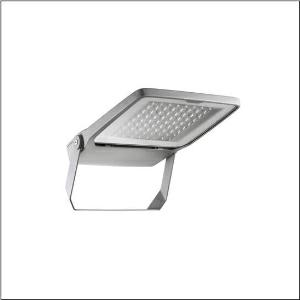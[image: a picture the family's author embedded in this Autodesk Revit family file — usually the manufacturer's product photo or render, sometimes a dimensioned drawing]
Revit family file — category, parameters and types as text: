
# Revit family: floodlight_fl_20_mini___pl43_5xa7671c2a1ac_d5d9
name_source: partatom
category: Lighting Fixtures
units: mm (PartAtom-declared; Revit-internal decimal feet)

## family parameters
Cut with Voids When Loaded = No
Host = Face
Light Source = No
Part Type = Normal
Room Calculation Point = No
Round Connector Dimension = Use Diameter
Shared = No

## types (1)
- Floodlight FL 20 mini  PL43 (1 x LED 4000K / CRI = 70 (unbekannt), 13030 lm, 4000K)
    Apparent Load = 96 VA
    CIE Flux Codes = 32 74 99 100 100
    Color Rendering = 70
    Color Temperature = 4000K
    Default Elevation = 1800 mm
    Description = Floodlight FL 20 mini, floodlight, primary light control with lens, of plastic, primary optical cover: protective disc, of toughened safety glass, transparent, light distribution: PL43, light emission: direct distribution, primary light characteristic: asymmetric, installation type: surface-mounted, LED, High Power LED, rated luminous flux: 13.030lm, luminous efficacy: 136lm/W, light colour: 740, colour temperature: 4000K, control gear: ECG Basic, control: power reduction, overheat protection, electronic power reduction, with terminal, 5-pole, max. 2.5mm², mains connection: 220..240V, AC, 50/60Hz, rated input power: 96W, LED unit, of diecast aluminium, powder-coated, Siteco® metallic grey (DB 702S), corrosivity category C5 mid according to DIN EN ISO 12944, incl. 1x M20 cable gland for cable Ø 6.5..12mm, length: 446mm, width: 355mm, height: 62mm, housing frame, of diecast aluminium, powder-coated, Siteco® metallic grey (DB 702S), mounting bracket, of steel, powder-coated, Siteco® metallic grey (DB 702S), ON/OFF, protection rating (complete): IP66, insulation class (complete): insulation class I (protective earthing), certification: CE, ENEC, VDE, protection symbol: D, permissible operating ambient temperature: -40..+40°C, permissible operating ambient temperature for outdoor applications: -40..+50°C, standard: DIN EN 12944, packaging unit: 1 piece

Light Distribution: PL43
    Height = 62 mm  [stored 0.203412 ft]
    Lamp = 1 x LED 4000K / CRI >= 70 (unbekannt)
    Lamp Light Flux = 13030 lm
    Lamp count = 1
    Length = 467 mm
    Luminous efficacy = 136 lm/W
    Manufacturer = Siteco
    ModVariant = No
    Model = 5XA7671C2A1AC
    Mounting Place = Wall
    Mounting Type = Surface mounted
    Number of Poles = 1
    OnlyDefault = Yes
    Power Factor = 1
    Product Name = Floodlight FL 20 mini | PL43
    Product group = floodlight | wall mounted
    ProductGroupID = 2001
    Protection Class = Protection class I
    Protection Degree = IP 66
    RLX_Detail_Level = 1
    RLX_Emergency_Light_Flux = 0 lm
    RLX_Emergency_Type = 0
    RLX_Emergency_Type_DB = No
    RlxData = <blob elided: 70897 chars, md5=3b5f903c>
    Socket = socket
    Standby Power = 0 W
    System Light Flux = 13030 lm
    System Power = 96 W
    Type Comments = Product without accessories
    Type Image = l_1005948.jpg
    URL = http://relux.com
    VarID = ---
    Voltage = 0 V
    Weight = 0.00 kg
    Width = 335 mm

note: [stored X ft] marks values corroborated as IEEE doubles in the binary element streams (Revit-internal decimal feet)

## geometry (parser evidence)
native form markers: Blend x4, Sweep x13
no freeform markers — native parametric forms only
